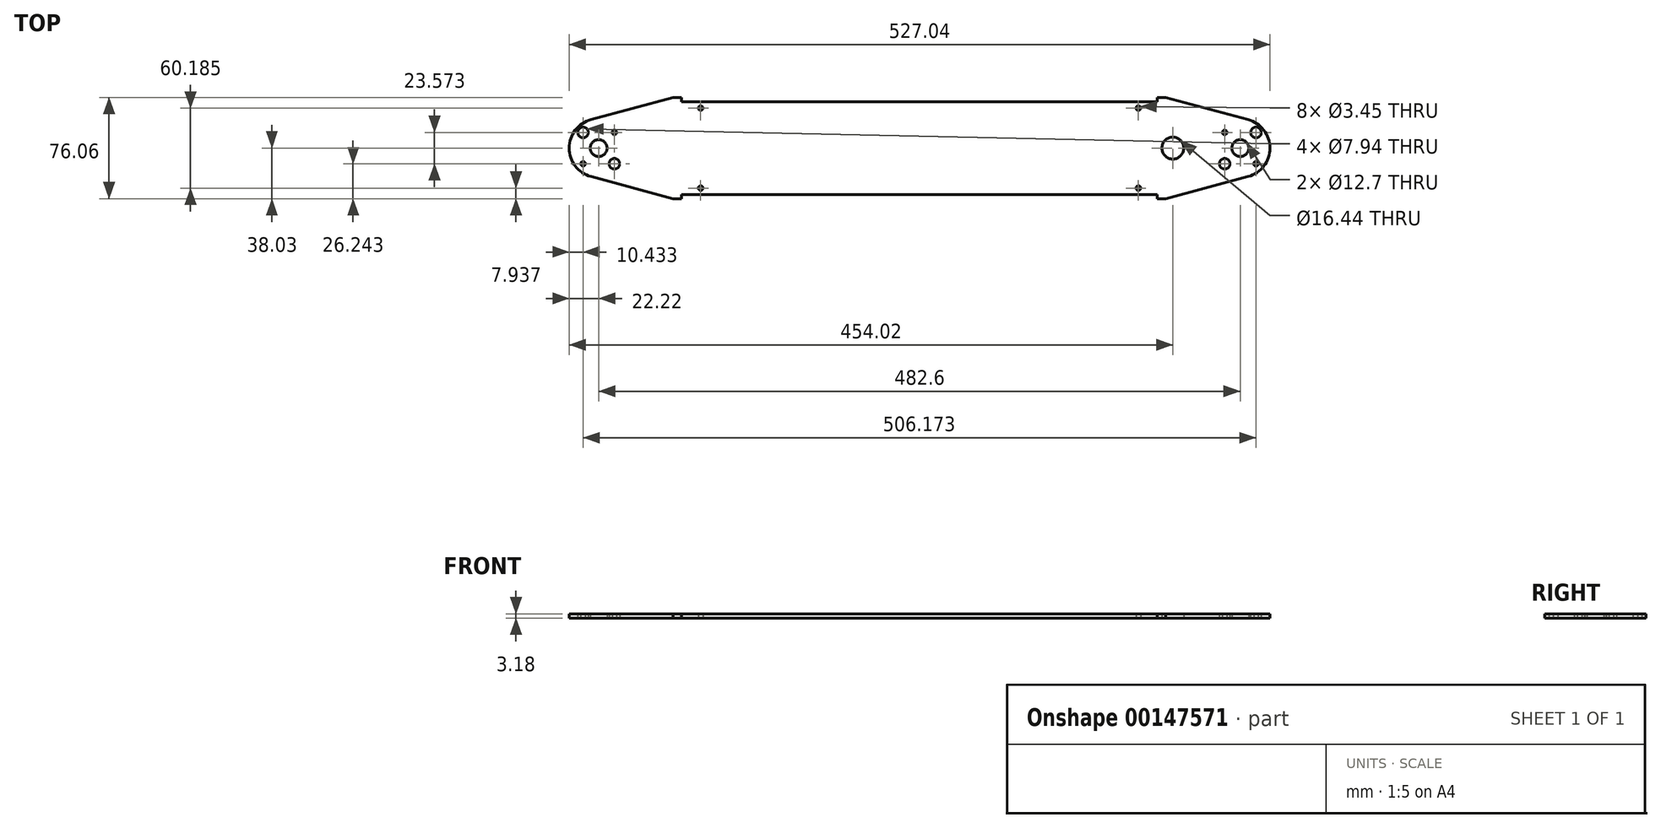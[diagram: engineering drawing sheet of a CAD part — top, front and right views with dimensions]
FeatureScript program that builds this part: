
annotation { "Feature Type Name" : "Feature", "Feature Type Description" : "" }
export const myFeature = defineFeature(function(context is Context, id is Id, definition is map)
    precondition{}
    {
        {
            var Q0;
            Q0=qCreatedBy(makeId("Top.planeOp"),FACE);
            var sketch = newSketch(context, id + "F0", { "sketchPlane" : qUnion([Q0])});
            skPoint(sketch, "E0.rect.middle", {"position": v(0, 0) * mm});
            skCircle(sketch, "E1", {"center": v(0, 0) * mm, "radius": 11.11 * mm, "construction": true});
            skLineSegment(sketch, "E2.bottom", {"start": v(11.79, 11.79) * mm, "end": v(-11.79, 11.79) * mm, "construction": true});
            skLineSegment(sketch, "E2.left", {"start": v(11.79, 11.79) * mm, "end": v(11.79, -11.79) * mm, "construction": true});
            skLineSegment(sketch, "E2.right", {"start": v(-11.79, 11.79) * mm, "end": v(-11.79, -11.79) * mm, "construction": true});
            skCircle(sketch, "E3", {"center": v(11.79, 11.79) * mm, "radius": 5.56 * mm, "construction": true});
            skCircle(sketch, "E4", {"center": v(-11.79, 11.79) * mm, "radius": 1.73 * mm});
            skCircle(sketch, "E5", {"center": v(11.79, 11.79) * mm, "radius": 3.97 * mm});
            skCircle(sketch, "E6", {"center": v(11.79, -11.79) * mm, "radius": 1.73 * mm});
            skCircle(sketch, "E7", {"center": v(-11.79, -11.79) * mm, "radius": 3.97 * mm});
            skArc(sketch, "E8", {"start": v(-488.35, 21.47) * mm, "mid": v(-504.83, 0) * mm, "end": v(-488.35, -21.47) * mm});
            skLineSegment(sketch, "E9.bottom", {"start": v(-494.39, 11.79) * mm, "end": v(-470.81, 11.79) * mm, "construction": true});
            skLineSegment(sketch, "E9.top", {"start": v(-494.39, -11.79) * mm, "end": v(-470.81, -11.79) * mm, "construction": true});
            skLineSegment(sketch, "E9.left", {"start": v(-494.39, 11.79) * mm, "end": v(-494.39, -11.79) * mm, "construction": true});
            skLineSegment(sketch, "E9.right", {"start": v(-470.81, 11.79) * mm, "end": v(-470.81, -11.79) * mm, "construction": true});
            skCircle(sketch, "E10", {"center": v(-470.81, 11.79) * mm, "radius": 1.73 * mm});
            skCircle(sketch, "E11", {"center": v(-482.6, 0) * mm, "radius": 6.35 * mm});
            skCircle(sketch, "E12", {"center": v(-494.39, 11.79) * mm, "radius": 3.97 * mm});
            skCircle(sketch, "E13", {"center": v(-494.39, -11.79) * mm, "radius": 1.73 * mm});
            skCircle(sketch, "E14", {"center": v(-470.81, -11.79) * mm, "radius": 3.97 * mm});
            skLineSegment(sketch, "E15", {"start": v(0, 0) * mm, "end": v(-482.6, 0) * mm, "construction": true});
            skLineSegment(sketch, "E16", {"start": v(-488.35, -21.47) * mm, "end": v(-426.54, -38.03) * mm});
            skLineSegment(sketch, "E17", {"start": v(-488.35, 21.47) * mm, "end": v(-426.54, 38.03) * mm});
            skLineSegment(sketch, "E18", {"start": v(-420.2, -34.86) * mm, "end": v(-62.4, -34.86) * mm});
            skLineSegment(sketch, "E19", {"start": v(-420.2, 34.86) * mm, "end": v(-62.4, 34.86) * mm});
            skLineSegment(sketch, "E20", {"start": v(-420.2, 38.03) * mm, "end": v(-420.2, 34.86) * mm});
            skLineSegment(sketch, "E21", {"start": v(-420.2, 38.03) * mm, "end": v(-426.54, 38.03) * mm});
            skLineSegment(sketch, "E22", {"start": v(-420.2, -34.86) * mm, "end": v(-420.2, -38.03) * mm});
            skLineSegment(sketch, "E23", {"start": v(-420.2, -38.03) * mm, "end": v(-426.54, -38.03) * mm});
            skLineSegment(sketch, "E24", {"start": v(-62.4, -34.86) * mm, "end": v(-62.4, -38.03) * mm});
            skLineSegment(sketch, "E25", {"start": v(-62.4, -38.03) * mm, "end": v(-56.06, -38.03) * mm});
            skLineSegment(sketch, "E26", {"start": v(-62.4, 34.86) * mm, "end": v(-62.4, 38.03) * mm});
            skLineSegment(sketch, "E27", {"start": v(-62.4, 38.03) * mm, "end": v(-56.06, 38.03) * mm});
            skLineSegment(sketch, "E28", {"start": v(-56.06, -38.03) * mm, "end": v(5.75, -21.47) * mm});
            skLineSegment(sketch, "E29", {"start": v(5.75, 21.47) * mm, "end": v(-56.06, 38.03) * mm});
            skArc(sketch, "E30", {"start": v(5.75, -21.47) * mm, "mid": v(22.23, 0) * mm, "end": v(5.75, 21.47) * mm});
            skLineSegment(sketch, "E31", {"start": v(-420.2, 34.86) * mm, "end": v(-420.2, 30.1) * mm, "construction": true});
            skLineSegment(sketch, "E32", {"start": v(-420.2, 30.1) * mm, "end": v(-405.9, 30.1) * mm, "construction": true});
            skLineSegment(sketch, "E33", {"start": v(-420.2, -34.86) * mm, "end": v(-420.2, -30.1) * mm, "construction": true});
            skLineSegment(sketch, "E34", {"start": v(-420.2, -30.1) * mm, "end": v(-405.9, -30.1) * mm, "construction": true});
            skLineSegment(sketch, "E35", {"start": v(-62.4, -34.86) * mm, "end": v(-62.4, -30.1) * mm, "construction": true});
            skLineSegment(sketch, "E36", {"start": v(-62.4, -30.1) * mm, "end": v(-76.7, -30.1) * mm, "construction": true});
            skLineSegment(sketch, "E37", {"start": v(-62.4, 34.86) * mm, "end": v(-62.4, 30.1) * mm, "construction": true});
            skLineSegment(sketch, "E38", {"start": v(-62.4, 30.1) * mm, "end": v(-76.7, 30.1) * mm, "construction": true});
            skCircle(sketch, "E39", {"center": v(-405.9, 30.1) * mm, "radius": 1.73 * mm});
            skCircle(sketch, "E40", {"center": v(-76.7, 30.1) * mm, "radius": 1.73 * mm});
            skCircle(sketch, "E41", {"center": v(-76.7, -30.1) * mm, "radius": 1.73 * mm});
            skCircle(sketch, "E42", {"center": v(-405.9, -30.1) * mm, "radius": 1.73 * mm});
            skLineSegment(sketch, "E43", {"start": v(-11.79, -11.79) * mm, "end": v(11.79, -11.79) * mm, "construction": true});
            skLineSegment(sketch, "E44", {"start": v(-241.3, -34.86) * mm, "end": v(-241.3, 0) * mm, "construction": true});
            skLineSegment(sketch, "E45", {"start": v(-241.3, 0) * mm, "end": v(-241.3, 34.86) * mm, "construction": true});
            skCircle(sketch, "E46", {"center": v(-50.8, 0) * mm, "radius": 8.22 * mm});
            skCircle(sketch, "E47", {"center": v(0, 0) * mm, "radius": 6.35 * mm});
            skCircle(sketch, "E48", {"center": v(-494.39, 11.79) * mm, "radius": 5.56 * mm, "construction": true});
            skLineSegment(sketch, "E49", {"start": v(-488.35, 21.47) * mm, "end": v(-457.45, 21.47) * mm, "construction": true});
            skLineSegment(sketch, "E50", {"start": v(-457.45, 21.47) * mm, "end": v(-457.45, 29.75) * mm, "construction": true});
            skSolve(sketch);
        }
        {
            var Q0;
            Q0=qSketchRegion(id+"F0",true);
            extrude(context, id + "F1", {"entities" : qUnion([Q0]), "depth" : 3.17 * mm});
        }
    });
